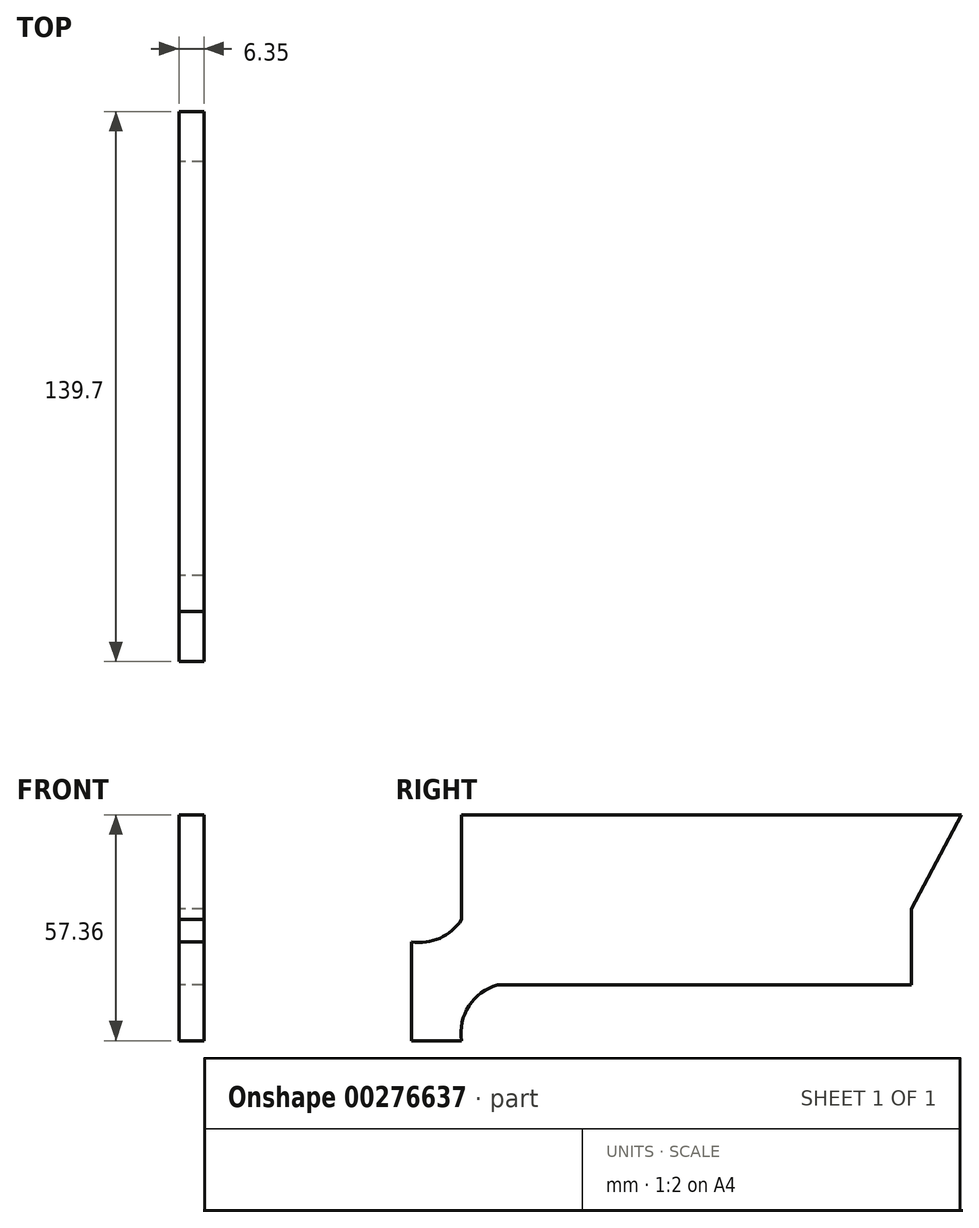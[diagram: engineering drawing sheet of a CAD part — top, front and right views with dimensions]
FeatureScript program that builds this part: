
annotation { "Feature Type Name" : "Feature", "Feature Type Description" : "" }
export const myFeature = defineFeature(function(context is Context, id is Id, definition is map)
    precondition{}
    {
        {
            var Q0;
            Q0=qCreatedBy(makeId("Right.planeOp"),FACE);
            var sketch = newSketch(context, id + "F0", { "sketchPlane" : qUnion([Q0])});
            skLineSegment(sketch, "E0", {"start": v(10.2, -51.08) * mm, "end": v(22.9, -51.08) * mm});
            skLineSegment(sketch, "E1", {"start": v(10.2, -51.08) * mm, "end": v(10.2, -25.68) * mm});
            skLineSegment(sketch, "E2", {"start": v(22.9, -20.33) * mm, "end": v(22.9, 6.28) * mm});
            skArc(sketch, "E3.trimOffspring", {"start": v(22.9, -20.33) * mm, "mid": v(17.39, -25.03) * mm, "end": v(10.2, -25.96) * mm});
            skLineSegment(sketch, "E4", {"start": v(22.9, 6.28) * mm, "end": v(149.9, 6.28) * mm});
            skLineSegment(sketch, "E5", {"start": v(32.09, -36.9) * mm, "end": v(137.2, -36.9) * mm});
            skArc(sketch, "E6", {"start": v(32.09, -36.9) * mm, "mid": v(24.8, -42.24) * mm, "end": v(22.9, -51.08) * mm});
            skLineSegment(sketch, "E7", {"start": v(137.2, -36.9) * mm, "end": v(32.09, -36.9) * mm});
            skLineSegment(sketch, "E8", {"start": v(149.9, 6.28) * mm, "end": v(137.2, -17.6) * mm});
            skLineSegment(sketch, "E9", {"start": v(137.2, -17.6) * mm, "end": v(137.2, -36.9) * mm});
            skLineSegment(sketch, "E10", {"start": v(149.62, 11.35) * mm, "end": v(22.73, 11.35) * mm});
            skLineSegment(sketch, "E11", {"start": v(149.9, 6.28) * mm, "end": v(137.2, 6.28) * mm});
            skSolve(sketch);
        }
        {
            var Q0;
            Q0 = qSketchRegion(id + "F6bFiV6ZGmyI6xi_0", true);
            var Q1;
            {var subQ2=sQuery(id+"F0.wireOp",EDGE,"E0");Q1=makeQuery(id+"F0.imprint","IMPRINT",FACE,{"disambiguationData":[TD([[makeQuery(id+"F0.imprint","IMPRINT",EDGE,{"derivedFrom":subQ2}),1.0]])]});}
            extrude(context, id + "F1", {"entities" : qUnion([Q0, Q1]), "depth" : 6.35 * mm});
        }
    });
